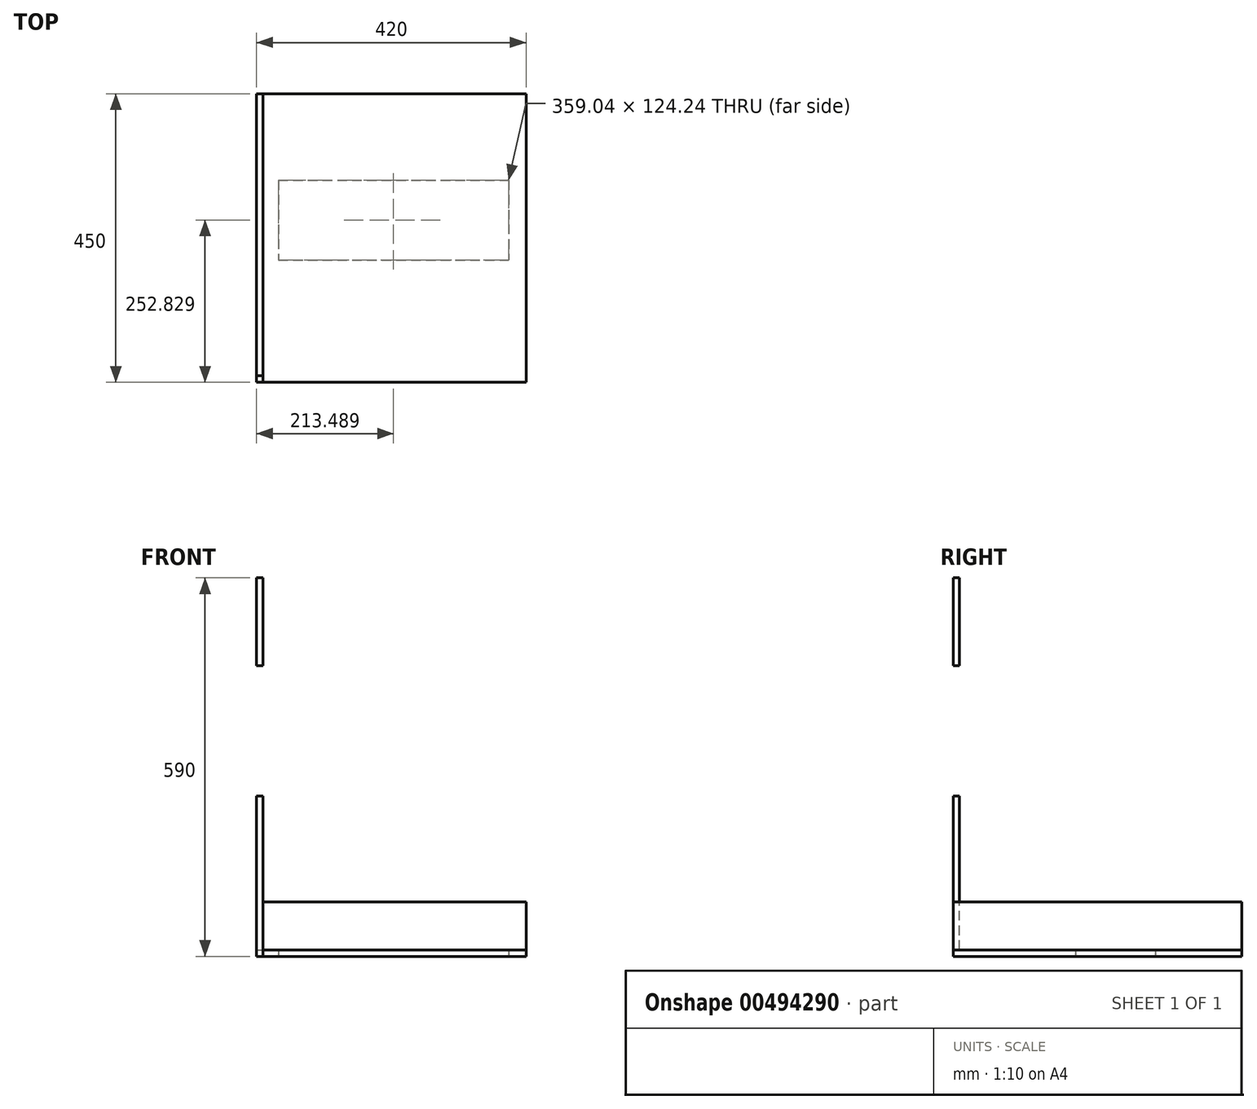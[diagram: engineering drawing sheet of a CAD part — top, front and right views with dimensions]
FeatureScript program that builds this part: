
annotation { "Feature Type Name" : "Feature", "Feature Type Description" : "" }
export const myFeature = defineFeature(function(context is Context, id is Id, definition is map)
    precondition{}
    {
        {
            var Q0;
            Q0=qCreatedBy(makeId("Right.planeOp"),FACE);
            var sketch = newSketch(context, id + "F0", { "sketchPlane" : qUnion([Q0])});
            skLineSegment(sketch, "E0.bottom", {"start": v(0, 0) * mm, "end": v(450, 0) * mm});
            skLineSegment(sketch, "E0.top", {"start": v(0, 600) * mm, "end": v(450, 600) * mm});
            skLineSegment(sketch, "E0.left", {"start": v(0, 0) * mm, "end": v(0, 600) * mm});
            skLineSegment(sketch, "E0.right", {"start": v(450, 0) * mm, "end": v(450, 600) * mm});
            skLineSegment(sketch, "E1.top", {"start": v(0, 10) * mm, "end": v(450, 10) * mm});
            skLineSegment(sketch, "E1.left", {"start": v(0, 0) * mm, "end": v(0, 10) * mm});
            skLineSegment(sketch, "E1.right", {"start": v(450, 0) * mm, "end": v(450, 10) * mm});
            skLineSegment(sketch, "E2.bottom", {"start": v(450, 600) * mm, "end": v(440, 600) * mm});
            skLineSegment(sketch, "E2.top", {"start": v(450, 10) * mm, "end": v(440, 10) * mm});
            skLineSegment(sketch, "E2.left", {"start": v(450, 600) * mm, "end": v(450, 10) * mm});
            skLineSegment(sketch, "E2.right", {"start": v(440, 600) * mm, "end": v(440, 10) * mm});
            skLineSegment(sketch, "E3.bottom", {"start": v(0, 600) * mm, "end": v(440, 600) * mm});
            skLineSegment(sketch, "E3.top", {"start": v(0, 590) * mm, "end": v(440, 590) * mm});
            skLineSegment(sketch, "E3.left", {"start": v(0, 600) * mm, "end": v(0, 590) * mm});
            skLineSegment(sketch, "E3.right", {"start": v(440, 600) * mm, "end": v(440, 590) * mm});
            skLineSegment(sketch, "E4.bottom", {"start": v(0, 10) * mm, "end": v(10, 10) * mm});
            skLineSegment(sketch, "E4.top", {"start": v(0, 250) * mm, "end": v(10, 250) * mm});
            skLineSegment(sketch, "E4.left", {"start": v(0, 10) * mm, "end": v(0, 250) * mm});
            skLineSegment(sketch, "E4.right", {"start": v(10, 10) * mm, "end": v(10, 250) * mm});
            skLineSegment(sketch, "E5.bottom", {"start": v(0, 590) * mm, "end": v(10, 590) * mm});
            skLineSegment(sketch, "E5.top", {"start": v(0, 453.23) * mm, "end": v(10, 453.23) * mm});
            skLineSegment(sketch, "E5.left", {"start": v(0, 590) * mm, "end": v(0, 453.23) * mm});
            skLineSegment(sketch, "E5.right", {"start": v(10, 590) * mm, "end": v(10, 453.23) * mm});
            skSolve(sketch);
        }
        {
            var Q0;
            Q0=makeQuery(id+"F0.imprint","IMPRINT",FACE,{"disambiguationData":[TD([[makeQuery(id+"F0.imprint","IMPRINT",EDGE,{"derivedFrom":sQuery(id+"F0.wireOp",EDGE,"E5.bottom")}),-1.0]])]});
            var Q1;
            Q1=makeQuery(id+"F0.imprint","IMPRINT",FACE,{"disambiguationData":[TD([[makeQuery(id+"F0.imprint","IMPRINT",EDGE,{"derivedFrom":sQuery(id+"F0.wireOp",EDGE,"E2.bottom")}),1.0]])]});
            var Q2;
            Q2=makeQuery(id+"F0.imprint","IMPRINT",FACE,{"disambiguationData":[TD([[makeQuery(id+"F0.imprint","IMPRINT",EDGE,{"derivedFrom":sQuery(id+"F0.wireOp",EDGE,"E3.bottom")}),-1.0]])]});
            var Q3;
            Q3=makeQuery(id+"F0.imprint","IMPRINT",FACE,{"disambiguationData":[TD([[makeQuery(id+"F0.imprint","IMPRINT",EDGE,{"derivedFrom":sQuery(id+"F0.wireOp",EDGE,"E4.bottom")}),1.0]])]});
            var Q4;
            Q4=makeQuery(id+"F0.imprint","IMPRINT",FACE,{"disambiguationData":[TD([[makeQuery(id+"F0.imprint","IMPRINT",EDGE,{"derivedFrom":sQuery(id+"F0.wireOp",EDGE,"E0.bottom")}),1.0]])]});
            extrude(context, id + "F1", {"entities" : qUnion([Q0, Q1, Q2, Q3, Q4]), "depth" : 410 * mm});
        }
        {
            var Q0;
            Q0=makeQuery(id+"F0.imprint","IMPRINT",FACE,{"disambiguationData":[TD([[makeQuery(id+"F0.imprint","IMPRINT",EDGE,{"derivedFrom":sQuery(id+"F0.wireOp",EDGE,"E3.bottom")}),-1.0]])]});
            var Q1;
            Q1=makeQuery(id+"F0.imprint","IMPRINT",FACE,{"disambiguationData":[TD([[makeQuery(id+"F0.imprint","IMPRINT",EDGE,{"derivedFrom":sQuery(id+"F0.wireOp",EDGE,"E5.bottom")}),-1.0]])]});
            var Q2;
            Q2=makeQuery(id+"F0.imprint","IMPRINT",FACE,{"disambiguationData":[TD([[makeQuery(id+"F0.imprint","IMPRINT",EDGE,{"derivedFrom":sQuery(id+"F0.wireOp",EDGE,"E2.bottom")}),1.0]])]});
            var Q3;
            Q3=makeQuery(id+"F0.imprint","IMPRINT",FACE,{"disambiguationData":[TD([[makeQuery(id+"F0.imprint","IMPRINT",EDGE,{"derivedFrom":sQuery(id+"F0.wireOp",EDGE,"E4.bottom")}),1.0]])]});
            var Q4;
            Q4=makeQuery(id+"F0.imprint","IMPRINT",FACE,{"disambiguationData":[TD([[makeQuery(id+"F0.imprint","IMPRINT",EDGE,{"derivedFrom":sQuery(id+"F0.wireOp",EDGE,"E0.bottom")}),1.0]])]});
            var Q5;
            Q5=makeQuery(id+"F0.imprint","IMPRINT",FACE,{"disambiguationData":[TD([[makeQuery(id+"F0.imprint","IMPRINT",EDGE,{"derivedFrom":sQuery(id+"F0.wireOp",EDGE,"E0.left")}),-1.0]])]});
            extrude(context, id + "F2", {"entities" : qUnion([Q0, Q1, Q2, Q3, Q4, Q5]), "oppositeDirection" : true, "depth" : 10 * mm});
        }
        {
            var Q0;
            Q0=makeQuery(id+"F2.opExtrude","CAP_FACE",FACE,{"disambiguationData":[OSD([sQuery(id+"F0.wireOp",EDGE,"E0.left"),sQuery(id+"F0.wireOp",EDGE,"E0.bottom"),sQuery(id+"F0.wireOp",EDGE,"E1.left"),sQuery(id+"F0.wireOp",EDGE,"E1.right"),sQuery(id+"F0.wireOp",EDGE,"E2.bottom"),sQuery(id+"F0.wireOp",EDGE,"E2.left"),sQuery(id+"F0.wireOp",EDGE,"E3.bottom"),sQuery(id+"F0.wireOp",EDGE,"E3.left"),sQuery(id+"F0.wireOp",EDGE,"E4.left"),sQuery(id+"F0.wireOp",EDGE,"E5.left")])],"isStart":false});
            var sketch = newSketch(context, id + "F3", { "sketchPlane" : qUnion([Q0])});
            skCircle(sketch, "E6", {"center": v(-250, 220) * mm, "radius": 5 * mm});
            skSolve(sketch);
        }
        {
            var Q0;
            Q0 = qSketchRegion(id + "F3", true);
            extrude(context, id + "F4", {"entities" : qUnion([Q0]), "operationType" : NewBodyOperationType.REMOVE, "oppositeDirection" : true, "depth" : 25 * mm});
        }
        {
            var Q0;
            Q0=makeQuery(id+"F1.opExtrude","SWEPT_FACE",FACE,{"disambiguationData":[OSD([sQuery(id+"F0.wireOp",EDGE,"E0.bottom")])]});
            var sketch = newSketch(context, id + "F5", { "sketchPlane" : qUnion([Q0])});
            skLineSegment(sketch, "E7.bottom", {"start": v(410, -190.71) * mm, "end": v(0, -190.71) * mm});
            skLineSegment(sketch, "E7.top", {"start": v(410, -314.95) * mm, "end": v(0, -314.95) * mm});
            skLineSegment(sketch, "E7.left", {"start": v(410, -190.71) * mm, "end": v(410, -314.95) * mm});
            skLineSegment(sketch, "E7.right", {"start": v(0, -190.71) * mm, "end": v(0, -314.95) * mm});
            skSolve(sketch);
        }
        {
            var Q0;
            Q0=makeQuery(id+"F5.imprint","IMPRINT",FACE,{"disambiguationData":[TD([[makeQuery(id+"F5.imprint","IMPRINT",EDGE,{"derivedFrom":sQuery(id+"F5.wireOp",EDGE,"E7.bottom")}),1.0]])]});
            var sketch = newSketch(context, id + "F6", { "sketchPlane" : qUnion([Q0])});
            skLineSegment(sketch, "E8.bottom", {"start": v(383, -189.76) * mm, "end": v(23.97, -189.76) * mm});
            skLineSegment(sketch, "E8.top", {"start": v(383, -316.25) * mm, "end": v(23.97, -316.25) * mm});
            skLineSegment(sketch, "E8.left", {"start": v(383, -189.76) * mm, "end": v(383, -316.25) * mm});
            skLineSegment(sketch, "E8.right", {"start": v(23.97, -189.76) * mm, "end": v(23.97, -316.25) * mm});
            skSolve(sketch);
        }
        {
            var Q0;
            {var subQ0=sQuery(id+"F6.wireOp",EDGE,"E8.left");var subQ1=makeQuery(id+"F5.imprint","IMPRINT",EDGE,{"derivedFrom":sQuery(id+"F5.wireOp",EDGE,"E7.bottom")});var subQ2=makeQuery(id+"F6.imprint","INTERSECT",VERTEX,{"derivedFrom":[subQ1,subQ0]});Q0=makeQuery(id+"F6.imprint","IMPRINT",FACE,{"disambiguationData":[TD([[makeQuery(id+"F6.imprint","IMPRINT",EDGE,{"disambiguationData":[TD([[subQ2,-1.0]])],"derivedFrom":subQ0}),-1.0]])]});}
            extrude(context, id + "F7", {"entities" : qUnion([Q0]), "operationType" : NewBodyOperationType.REMOVE, "oppositeDirection" : true, "depth" : 25 * mm});
        }
        {
            var Q0;
            {var subQ0=sQuery(id+"F5.wireOp",EDGE,"E7.top");Q0=makeQuery(id+"F5.imprint","IMPRINT",FACE,{"disambiguationData":[TD([[makeQuery(id+"F5.imprint","IMPRINT",EDGE,{"derivedFrom":subQ0}),1.0]])]});}
            var Q1;
            {var subQ0=sQuery(id+"F5.wireOp",EDGE,"E7.bottom");Q1=makeQuery(id+"F5.imprint","IMPRINT",FACE,{"disambiguationData":[TD([[makeQuery(id+"F5.imprint","IMPRINT",EDGE,{"derivedFrom":subQ0}),-1.0]])]});}
            var Q2;
            Q2=makeQuery(id+"F5.imprint","IMPRINT",FACE,{"disambiguationData":[TD([[makeQuery(id+"F5.imprint","IMPRINT",EDGE,{"derivedFrom":sQuery(id+"F5.wireOp",EDGE,"E7.bottom")}),1.0]])]});
            extrude(context, id + "F8", {"entities" : qUnion([Q0, Q1, Q2]), "oppositeDirection" : true, "depth" : 85 * mm});
        }
    });
